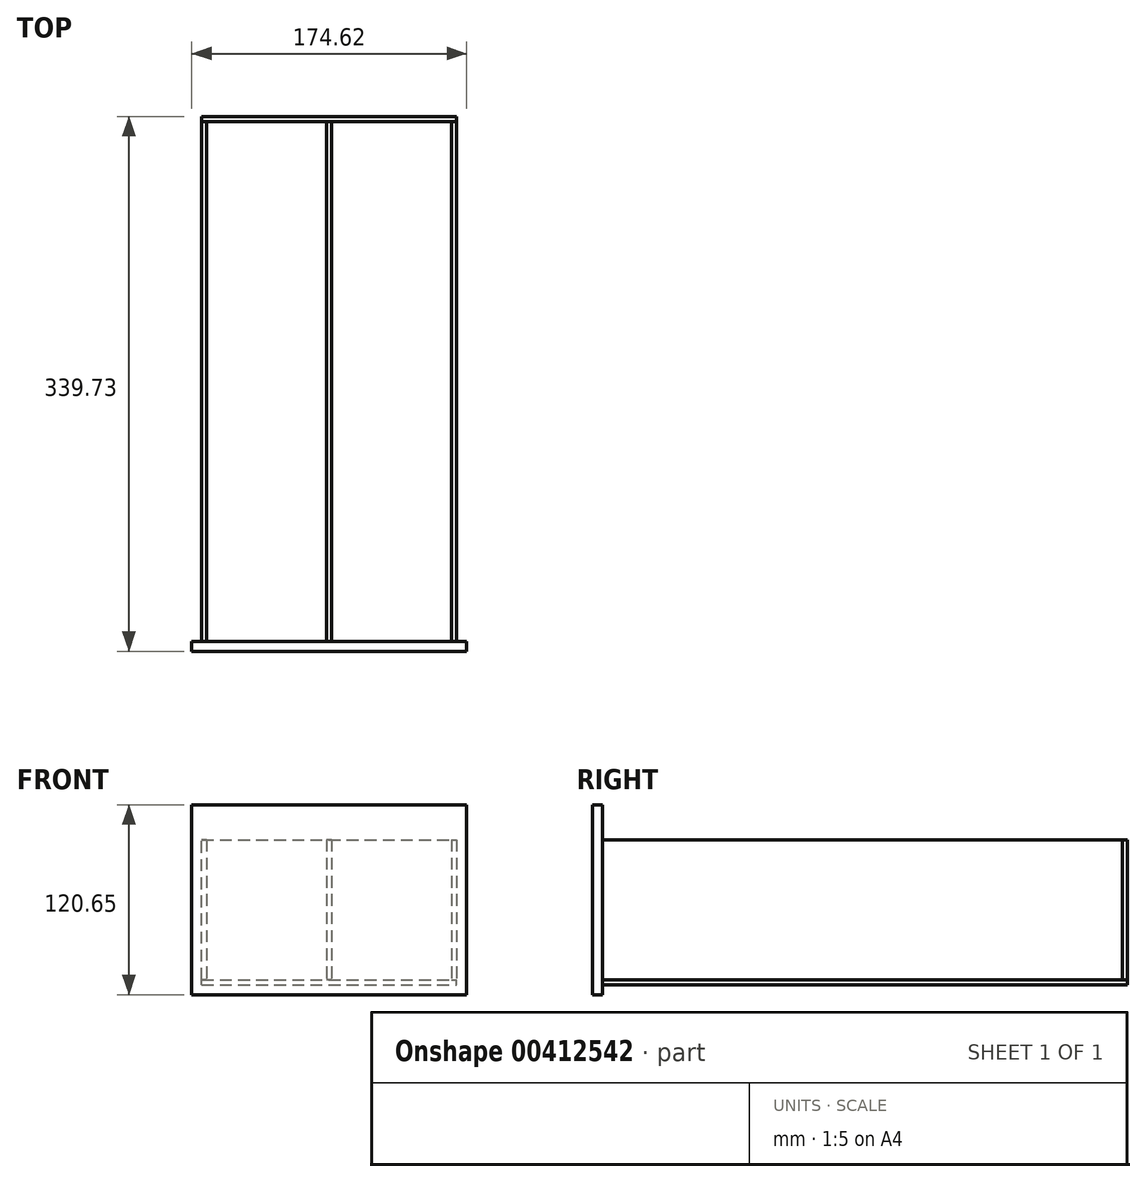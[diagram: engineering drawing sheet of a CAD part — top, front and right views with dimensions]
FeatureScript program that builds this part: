
annotation { "Feature Type Name" : "Feature", "Feature Type Description" : "" }
export const myFeature = defineFeature(function(context is Context, id is Id, definition is map)
    precondition{}
    {
        {
            var Q0;
            Q0=qCreatedBy(makeId("Front.planeOp"),FACE);
            var sketch = newSketch(context, id + "F0", { "sketchPlane" : qUnion([Q0])});
            skLineSegment(sketch, "E0.bottom", {"start": v(0, 0) * mm, "end": v(174.62, 0) * mm});
            skLineSegment(sketch, "E0.top", {"start": v(0, 120.65) * mm, "end": v(174.62, 120.65) * mm});
            skLineSegment(sketch, "E0.left", {"start": v(0, 0) * mm, "end": v(0, 120.65) * mm});
            skLineSegment(sketch, "E0.right", {"start": v(174.62, 0) * mm, "end": v(174.62, 120.65) * mm});
            skSolve(sketch);
        }
        {
            var Q0;
            Q0 = qSketchRegion(id + "F0", true);
            extrude(context, id + "F1", {"entities" : qUnion([Q0]), "depth" : 6.35 * mm});
        }
        {
            var Q0;
            Q0=makeQuery(id+"F1.opExtrude","SWEPT_FACE",FACE,{"disambiguationData":[OSD([sQuery(id+"F0.wireOp",EDGE,"E0.right")])]});
            cPlane(context, id + "F2", {"entities" : qUnion([Q0]), "cplaneType" : CPlaneType.OFFSET, "offset" : 6.35 * mm, "oppositeDirection" : true, "width" : 152.4 * mm, "height" : 152.4 * mm});
        }
        {
            var Q0;
            Q0=qCreatedBy(id+"F2.planeOp",FACE);
            var sketch = newSketch(context, id + "F3", { "sketchPlane" : qUnion([Q0])});
            skLineSegment(sketch, "E1.bottom", {"start": v(0, 98.42) * mm, "end": v(330.2, 98.42) * mm});
            skLineSegment(sketch, "E1.top", {"start": v(0, 9.52) * mm, "end": v(330.2, 9.52) * mm});
            skLineSegment(sketch, "E1.left", {"start": v(0, 98.42) * mm, "end": v(0, 9.53) * mm});
            skLineSegment(sketch, "E1.right", {"start": v(330.2, 98.42) * mm, "end": v(330.2, 9.52) * mm});
            skSolve(sketch);
        }
        {
            var Q0;
            Q0 = qSketchRegion(id + "F3", true);
            extrude(context, id + "F4", {"entities" : qUnion([Q0]), "oppositeDirection" : true, "depth" : 3.17 * mm});
        }
        {
            var Q0;
            Q0=makeQuery(id+"F1.opExtrude","SWEPT_FACE",FACE,{"disambiguationData":[OSD([sQuery(id+"F0.wireOp",EDGE,"E0.left")])]});
            cPlane(context, id + "F5", {"entities" : qUnion([Q0]), "cplaneType" : CPlaneType.OFFSET, "offset" : 6.35 * mm, "oppositeDirection" : true, "width" : 152.4 * mm, "height" : 152.4 * mm});
        }
        {
            var Q0;
            Q0=qCreatedBy(id+"F5.planeOp",FACE);
            var sketch = newSketch(context, id + "F6", { "sketchPlane" : qUnion([Q0])});
            skLineSegment(sketch, "E2.bottom", {"start": v(0, 98.43) * mm, "end": v(-330.2, 98.42) * mm});
            skLineSegment(sketch, "E2.top", {"start": v(0, 9.53) * mm, "end": v(-330.2, 9.52) * mm});
            skLineSegment(sketch, "E2.left", {"start": v(0, 98.43) * mm, "end": v(0, 9.53) * mm});
            skLineSegment(sketch, "E2.right", {"start": v(-330.2, 98.42) * mm, "end": v(-330.2, 9.52) * mm});
            skSolve(sketch);
        }
        {
            var Q0;
            Q0 = qSketchRegion(id + "F6", true);
            extrude(context, id + "F7", {"entities" : qUnion([Q0]), "oppositeDirection" : true, "depth" : 3.17 * mm});
        }
        {
            var Q0;
            Q0=makeQuery(id+"F4.opExtrude","SWEPT_FACE",FACE,{"disambiguationData":[OSD([sQuery(id+"F3.wireOp",EDGE,"E1.right")])]});
            var sketch = newSketch(context, id + "F8", { "sketchPlane" : qUnion([Q0])});
            skPoint(sketch, "E3.0", {"position": v(-168.27, 98.42) * mm});
            skPoint(sketch, "E4.0", {"position": v(-6.35, 98.42) * mm});
            skPoint(sketch, "E5.0", {"position": v(-6.35, 9.52) * mm});
            skPoint(sketch, "E6.0", {"position": v(-168.28, 9.52) * mm});
            skLineSegment(sketch, "E7", {"start": v(-168.28, 98.42) * mm, "end": v(-168.28, 9.52) * mm});
            skLineSegment(sketch, "E8", {"start": v(-6.35, 9.52) * mm, "end": v(-168.28, 9.52) * mm});
            skLineSegment(sketch, "E9", {"start": v(-6.35, 9.52) * mm, "end": v(-6.35, 98.42) * mm});
            skLineSegment(sketch, "E10", {"start": v(-168.27, 98.42) * mm, "end": v(-6.35, 98.42) * mm});
            skSolve(sketch);
        }
        {
            var Q0;
            Q0 = qSketchRegion(id + "F8", true);
            extrude(context, id + "F9", {"entities" : qUnion([Q0]), "depth" : 3.17 * mm});
        }
        {
            var Q0;
            Q0=makeQuery(id+"F4.opExtrude","SWEPT_FACE",FACE,{"disambiguationData":[OSD([sQuery(id+"F3.wireOp",EDGE,"E1.top")])]});
            var sketch = newSketch(context, id + "F10", { "sketchPlane" : qUnion([Q0])});
            skPoint(sketch, "E11.0", {"position": v(6.35, 0) * mm});
            skPoint(sketch, "E12.0", {"position": v(168.28, 0) * mm});
            skPoint(sketch, "E13.0", {"position": v(168.28, -333.38) * mm});
            skPoint(sketch, "E14.0", {"position": v(6.35, -333.38) * mm});
            skLineSegment(sketch, "E15", {"start": v(6.35, 0) * mm, "end": v(168.28, 0) * mm});
            skLineSegment(sketch, "E16", {"start": v(168.28, 0) * mm, "end": v(168.28, -333.38) * mm});
            skLineSegment(sketch, "E17", {"start": v(168.28, -333.38) * mm, "end": v(6.35, -333.38) * mm});
            skLineSegment(sketch, "E18", {"start": v(6.35, -333.38) * mm, "end": v(6.35, 0) * mm});
            skSolve(sketch);
        }
        {
            var Q0;
            Q0 = qSketchRegion(id + "F10", true);
            extrude(context, id + "F11", {"entities" : qUnion([Q0]), "depth" : 3.17 * mm});
        }
        {
            var Q0;
            Q0=makeQuery(id+"F4.opExtrude","CAP_FACE",FACE,{"disambiguationData":[OSD([sQuery(id+"F3.wireOp",EDGE,"E1.bottom"),sQuery(id+"F3.wireOp",EDGE,"E1.top"),sQuery(id+"F3.wireOp",EDGE,"E1.left"),sQuery(id+"F3.wireOp",EDGE,"E1.right")])],"isStart":true});
            var Q1;
            Q1=makeQuery(id+"F7.opExtrude","CAP_FACE",FACE,{"disambiguationData":[OSD([sQuery(id+"F6.wireOp",EDGE,"E2.bottom"),sQuery(id+"F6.wireOp",EDGE,"E2.top"),sQuery(id+"F6.wireOp",EDGE,"E2.left"),sQuery(id+"F6.wireOp",EDGE,"E2.right")])],"isStart":true});
            cPlane(context, id + "F12", {"entities" : qUnion([Q0, Q1]), "cplaneType" : CPlaneType.MID_PLANE, "offset" : 25.4 * mm, "width" : 152.4 * mm, "height" : 152.4 * mm});
        }
        {
            var Q0;
            Q0=qCreatedBy(id+"F12.planeOp",FACE);
            var sketch = newSketch(context, id + "F13", { "sketchPlane" : qUnion([Q0])});
            skLineSegment(sketch, "E19.0.0", {"start": v(330.2, 9.52) * mm, "end": v(0, 9.53) * mm});
            skLineSegment(sketch, "E19.0.1", {"start": v(0, 9.53) * mm, "end": v(0, 98.43) * mm});
            skLineSegment(sketch, "E19.0.2", {"start": v(0, 98.43) * mm, "end": v(330.2, 98.42) * mm});
            skLineSegment(sketch, "E19.0.3", {"start": v(330.2, 98.42) * mm, "end": v(330.2, 9.52) * mm});
            skSolve(sketch);
        }
        {
            var Q0;
            Q0 = qSketchRegion(id + "F13", true);
            extrude(context, id + "F14", {"entities" : qUnion([Q0]), "endBound" : BoundingType.SYMMETRIC, "depth" : 3.17 * mm});
        }
    });
